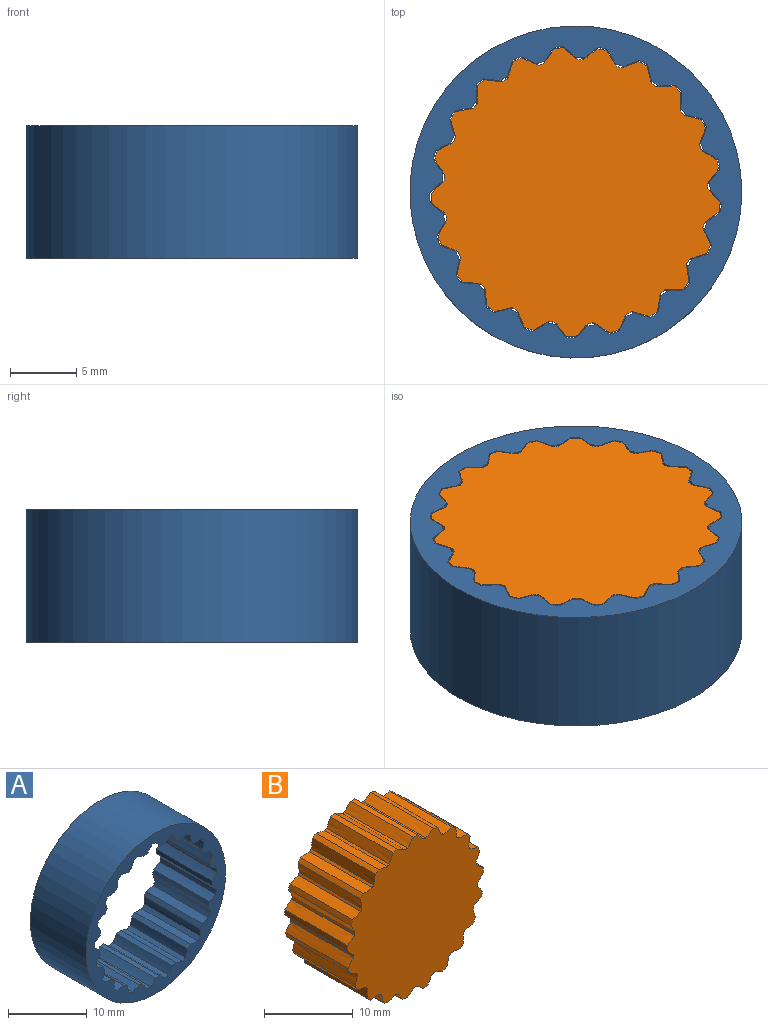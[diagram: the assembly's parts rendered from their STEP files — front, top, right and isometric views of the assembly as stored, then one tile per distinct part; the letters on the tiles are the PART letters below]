
ASSEMBLY  parts=2 mates=1
PART A: 87 faces, bbox 25x10x25 mm
  f0: cylinder r=10.11mm len=10mm, axis (0,1,0), area 6.9mm2, adj f20,f21,f38,f84
  f1: cylinder r=10.11mm len=10mm, axis (0,1,0), area 6.9mm2, adj f20,f21,f81,f86
  f2: cylinder r=10.11mm len=10mm, axis (0,1,0), area 6.9mm2, adj f20,f21,f78,f83
  f3: cylinder r=10.11mm len=10mm, axis (0,1,0), area 6.9mm2, adj f20,f21,f75,f80
  f4: cylinder r=10.11mm len=10mm, axis (0,1,0), area 6.9mm2, adj f20,f21,f72,f77
  f5: cylinder r=10.11mm len=10mm, axis (0,1,0), area 6.9mm2, adj f20,f21,f69,f74
  f6: cylinder r=10.11mm len=10mm, axis (0,1,0), area 6.9mm2, adj f20,f21,f66,f71
  f7: cylinder r=10.11mm len=10mm, axis (0,1,0), area 6.9mm2, adj f20,f21,f63,f68
  f8: cylinder r=10.11mm len=10mm, axis (0,1,0), area 6.9mm2, adj f20,f21,f60,f65
  f9: cylinder r=10.11mm len=10mm, axis (0,1,0), area 6.9mm2, adj f20,f21,f57,f62
  f10: cylinder r=10.11mm len=10mm, axis (0,1,0), area 6.9mm2, adj f20,f21,f54,f59
  f11: cylinder r=10.11mm len=10mm, axis (0,1,0), area 6.9mm2, adj f20,f21,f51,f56
  f12: cylinder r=10.11mm len=10mm, axis (0,1,0), area 6.9mm2, adj f20,f21,f48,f53
  f13: cylinder r=10.11mm len=10mm, axis (0,1,0), area 6.9mm2, adj f20,f21,f45,f50
  f14: cylinder r=10.11mm len=10mm, axis (0,1,0), area 6.9mm2, adj f20,f21,f42,f47
  f15: cylinder r=10.11mm len=10mm, axis (0,1,0), area 6.9mm2, adj f20,f21,f39,f44
  f16: cylinder r=10.11mm len=10mm, axis (0,1,0), area 6.9mm2, adj f20,f21,f35,f36
  f17: cylinder r=10.11mm len=10mm, axis (0,1,0), area 6.9mm2, adj f20,f21,f32,f33
  f18: cylinder r=10.11mm len=10mm, axis (0,1,0), area 6.9mm2, adj f20,f21,f26,f30
  f19: cylinder r=10.11mm len=10mm, axis (0,1,0), area 6.9mm2, adj f20,f21,f27,f41
  f20: plane 25x25mm, normal (0,-1,0), area 141.1mm2, adj f0,f1,f2,f3,f4,f5,f6,f7
  f21: plane 25x25mm, normal (0,1,0), area 141.1mm2, adj f0,f1,f2,f3,f4,f5,f6,f7
  f22: cylinder r=10.11mm len=10mm, axis (0,1,0), area 6.9mm2, adj f20,f21,f24,f29
  f23: cylinder r=12.5mm len=25mm, axis (0,1,0), area 785.4mm2, adj f20,f21
  f24: cylinder r=7.51mm len=10mm, axis (0,-1,0), area 12.7mm2, adj f20,f21,f22,f25
  f25: cylinder r=11mm len=10mm, axis (0,1,0), area 6.6mm2, adj f20,f21,f24,f26
  f26: cylinder r=7.51mm len=10mm, axis (0,1,0), area 12.7mm2, adj f18,f20,f21,f25
  f27: cylinder r=7.51mm len=10mm, axis (0,-1,0), area 12.7mm2, adj f19,f20,f21,f28
  f28: cylinder r=11mm len=10mm, axis (0,1,0), area 6.6mm2, adj f20,f21,f27,f29
  f29: cylinder r=7.51mm len=10mm, axis (0,1,0), area 12.7mm2, adj f20,f21,f22,f28
  f30: cylinder r=7.51mm len=10mm, axis (0,-1,0), area 12.7mm2, adj f18,f20,f21,f31
  f31: cylinder r=11mm len=10mm, axis (0,1,0), area 6.6mm2, adj f20,f21,f30,f32
  f32: cylinder r=7.51mm len=10mm, axis (0,1,0), area 12.7mm2, adj f17,f20,f21,f31
  f33: cylinder r=7.51mm len=10mm, axis (0,-1,0), area 12.7mm2, adj f17,f20,f21,f34
  f34: cylinder r=11mm len=10mm, axis (0,1,0), area 6.6mm2, adj f20,f21,f33,f35
  f35: cylinder r=7.51mm len=10mm, axis (0,1,0), area 12.7mm2, adj f16,f20,f21,f34
  f36: cylinder r=7.51mm len=10mm, axis (0,-1,0), area 12.7mm2, adj f16,f20,f21,f37
  f37: cylinder r=11mm len=10mm, axis (0,1,0), area 6.6mm2, adj f20,f21,f36,f38
  f38: cylinder r=7.51mm len=10mm, axis (0,1,0), area 12.7mm2, adj f0,f20,f21,f37
  f39: cylinder r=7.51mm len=10mm, axis (0,-1,0), area 12.7mm2, adj f15,f20,f21,f40
  f40: cylinder r=11mm len=10mm, axis (0,1,0), area 6.6mm2, adj f20,f21,f39,f41
  f41: cylinder r=7.51mm len=10mm, axis (0,1,0), area 12.7mm2, adj f19,f20,f21,f40
  f42: cylinder r=7.51mm len=10mm, axis (0,-1,0), area 12.7mm2, adj f14,f20,f21,f43
  f43: cylinder r=11mm len=10mm, axis (0,1,0), area 6.6mm2, adj f20,f21,f42,f44
  f44: cylinder r=7.51mm len=10mm, axis (0,1,0), area 12.7mm2, adj f15,f20,f21,f43
  f45: cylinder r=7.51mm len=10mm, axis (0,-1,0), area 12.7mm2, adj f13,f20,f21,f46
  f46: cylinder r=11mm len=10mm, axis (0,1,0), area 6.6mm2, adj f20,f21,f45,f47
  f47: cylinder r=7.51mm len=10mm, axis (0,1,0), area 12.7mm2, adj f14,f20,f21,f46
  f48: cylinder r=7.51mm len=10mm, axis (0,-1,0), area 12.7mm2, adj f12,f20,f21,f49
  f49: cylinder r=11mm len=10mm, axis (0,1,0), area 6.6mm2, adj f20,f21,f48,f50
  f50: cylinder r=7.51mm len=10mm, axis (0,1,0), area 12.7mm2, adj f13,f20,f21,f49
  f51: cylinder r=7.51mm len=10mm, axis (0,-1,0), area 12.7mm2, adj f11,f20,f21,f52
  f52: cylinder r=11mm len=10mm, axis (0,1,0), area 6.6mm2, adj f20,f21,f51,f53
  f53: cylinder r=7.51mm len=10mm, axis (0,1,0), area 12.7mm2, adj f12,f20,f21,f52
  f54: cylinder r=7.51mm len=10mm, axis (0,-1,0), area 12.7mm2, adj f10,f20,f21,f55
  f55: cylinder r=11mm len=10mm, axis (0,1,0), area 6.6mm2, adj f20,f21,f54,f56
  f56: cylinder r=7.51mm len=10mm, axis (0,1,0), area 12.7mm2, adj f11,f20,f21,f55
  f57: cylinder r=7.51mm len=10mm, axis (0,-1,0), area 12.7mm2, adj f9,f20,f21,f58
  f58: cylinder r=11mm len=10mm, axis (0,1,0), area 6.6mm2, adj f20,f21,f57,f59
  f59: cylinder r=7.51mm len=10mm, axis (0,1,0), area 12.7mm2, adj f10,f20,f21,f58
  f60: cylinder r=7.51mm len=10mm, axis (0,-1,0), area 12.7mm2, adj f8,f20,f21,f61
  f61: cylinder r=11mm len=10mm, axis (0,1,0), area 6.6mm2, adj f20,f21,f60,f62
  f62: cylinder r=7.51mm len=10mm, axis (0,1,0), area 12.7mm2, adj f9,f20,f21,f61
  f63: cylinder r=7.51mm len=10mm, axis (0,-1,0), area 12.7mm2, adj f7,f20,f21,f64
  f64: cylinder r=11mm len=10mm, axis (0,1,0), area 6.6mm2, adj f20,f21,f63,f65
  f65: cylinder r=7.51mm len=10mm, axis (0,1,0), area 12.7mm2, adj f8,f20,f21,f64
  f66: cylinder r=7.51mm len=10mm, axis (0,-1,0), area 12.7mm2, adj f6,f20,f21,f67
  f67: cylinder r=11mm len=10mm, axis (0,1,0), area 6.6mm2, adj f20,f21,f66,f68
  f68: cylinder r=7.51mm len=10mm, axis (0,1,0), area 12.7mm2, adj f7,f20,f21,f67
  f69: cylinder r=7.51mm len=10mm, axis (0,-1,0), area 12.7mm2, adj f5,f20,f21,f70
  f70: cylinder r=11mm len=10mm, axis (0,1,0), area 6.6mm2, adj f20,f21,f69,f71
  f71: cylinder r=7.51mm len=10mm, axis (0,1,0), area 12.7mm2, adj f6,f20,f21,f70
  f72: cylinder r=7.51mm len=10mm, axis (0,-1,0), area 12.7mm2, adj f4,f20,f21,f73
  f73: cylinder r=11mm len=10mm, axis (0,1,0), area 6.6mm2, adj f20,f21,f72,f74
  f74: cylinder r=7.51mm len=10mm, axis (0,1,0), area 12.7mm2, adj f5,f20,f21,f73
  f75: cylinder r=7.51mm len=10mm, axis (0,-1,0), area 12.7mm2, adj f3,f20,f21,f76
  f76: cylinder r=11mm len=10mm, axis (0,1,0), area 6.6mm2, adj f20,f21,f75,f77
  f77: cylinder r=7.51mm len=10mm, axis (0,1,0), area 12.7mm2, adj f4,f20,f21,f76
  f78: cylinder r=7.51mm len=10mm, axis (0,-1,0), area 12.7mm2, adj f2,f20,f21,f79
  f79: cylinder r=11mm len=10mm, axis (0,1,0), area 6.6mm2, adj f20,f21,f78,f80
  f80: cylinder r=7.51mm len=10mm, axis (0,1,0), area 12.7mm2, adj f3,f20,f21,f79
  f81: cylinder r=7.51mm len=10mm, axis (0,-1,0), area 12.7mm2, adj f1,f20,f21,f82
  f82: cylinder r=11mm len=10mm, axis (0,1,0), area 6.6mm2, adj f20,f21,f81,f83
  f83: cylinder r=7.51mm len=10mm, axis (0,1,0), area 12.7mm2, adj f2,f20,f21,f82
  f84: cylinder r=7.51mm len=10mm, axis (0,-1,0), area 12.7mm2, adj f0,f20,f21,f85
  f85: cylinder r=11mm len=10mm, axis (0,1,0), area 6.6mm2, adj f20,f21,f84,f86
  f86: cylinder r=7.51mm len=10mm, axis (0,1,0), area 12.7mm2, adj f1,f20,f21,f85
PART B: 86 faces, bbox 21.8x10x21.7 mm
  f0: cylinder r=9.95mm len=10mm, axis (0,1,0), area 3.6mm2, adj f21,f22,f25,f83
  f1: cylinder r=9.95mm len=10mm, axis (0,1,0), area 3.6mm2, adj f21,f22,f80,f85
  f2: cylinder r=9.95mm len=10mm, axis (0,1,0), area 3.6mm2, adj f21,f22,f77,f82
  f3: cylinder r=9.95mm len=10mm, axis (0,1,0), area 3.6mm2, adj f21,f22,f74,f79
  f4: cylinder r=9.95mm len=10mm, axis (0,1,0), area 3.6mm2, adj f21,f22,f71,f76
  f5: cylinder r=9.95mm len=10mm, axis (0,1,0), area 3.6mm2, adj f21,f22,f68,f73
  f6: cylinder r=9.95mm len=10mm, axis (0,1,0), area 3.6mm2, adj f21,f22,f65,f70
  f7: cylinder r=9.95mm len=10mm, axis (0,1,0), area 3.6mm2, adj f21,f22,f62,f67
  f8: cylinder r=9.95mm len=10mm, axis (0,1,0), area 3.6mm2, adj f21,f22,f59,f64
  f9: cylinder r=9.95mm len=10mm, axis (0,1,0), area 3.6mm2, adj f21,f22,f56,f61
  f10: cylinder r=9.95mm len=10mm, axis (0,1,0), area 3.6mm2, adj f21,f22,f53,f58
  f11: cylinder r=9.95mm len=10mm, axis (0,1,0), area 3.6mm2, adj f21,f22,f50,f55
  f12: cylinder r=9.95mm len=10mm, axis (0,1,0), area 3.6mm2, adj f21,f22,f47,f52
  f13: cylinder r=9.95mm len=10mm, axis (0,1,0), area 3.6mm2, adj f21,f22,f44,f49
  f14: cylinder r=9.95mm len=10mm, axis (0,1,0), area 3.6mm2, adj f21,f22,f41,f46
  f15: cylinder r=9.95mm len=10mm, axis (0,1,0), area 3.6mm2, adj f21,f22,f38,f43
  f16: cylinder r=9.95mm len=10mm, axis (0,1,0), area 3.6mm2, adj f21,f22,f35,f40
  f17: cylinder r=9.95mm len=10mm, axis (0,1,0), area 3.6mm2, adj f21,f22,f32,f37
  f18: cylinder r=9.95mm len=10mm, axis (0,1,0), area 3.6mm2, adj f21,f22,f29,f34
  f19: cylinder r=9.95mm len=10mm, axis (0,1,0), area 3.6mm2, adj f21,f22,f26,f31
  f20: cylinder r=9.95mm len=10mm, axis (0,1,0), area 3.6mm2, adj f21,f22,f23,f28
  f21: plane 21.78x21.73mm, normal (0,-1,0), area 343.1mm2, adj f0,f1,f2,f3,f4,f5,f6,f7
  f22: plane 21.78x21.73mm, normal (0,1,0), area 343.1mm2, adj f0,f1,f2,f3,f4,f5,f6,f7
  f23: extruded ~10x1.37mm, area 14.1mm2, adj f20,f21,f22,f24
  f24: cylinder r=10.9mm len=10mm, axis (0,1,0), area 6.9mm2, adj f21,f22,f23,f25
  f25: extruded ~10x1.39mm, area 14.1mm2, adj f0,f21,f22,f24
  f26: extruded ~10x1.22mm, area 14.1mm2, adj f19,f21,f22,f27
  f27: cylinder r=10.9mm len=10mm, axis (0,1,0), area 6.9mm2, adj f21,f22,f26,f28
  f28: extruded ~10x1.27mm, area 14.1mm2, adj f20,f21,f22,f27
  f29: extruded ~10x1.03mm, area 14.1mm2, adj f18,f21,f22,f30
  f30: cylinder r=10.9mm len=10mm, axis (0,1,0), area 6.9mm2, adj f21,f22,f29,f31
  f31: extruded ~10x1.03mm, area 14.1mm2, adj f19,f21,f22,f30
  f32: extruded ~10x1.27mm, area 14.1mm2, adj f17,f21,f22,f33
  f33: cylinder r=10.9mm len=10mm, axis (0,1,0), area 6.9mm2, adj f21,f22,f32,f34
  f34: extruded ~10x1.22mm, area 14.1mm2, adj f18,f21,f22,f33
  f35: extruded ~10x1.39mm, area 14.1mm2, adj f16,f21,f22,f36
  f36: cylinder r=10.9mm len=10mm, axis (0,1,0), area 6.9mm2, adj f21,f22,f35,f37
  f37: extruded ~10x1.37mm, area 14.1mm2, adj f17,f21,f22,f36
  f38: extruded ~10x1.39mm, area 14.1mm2, adj f15,f21,f22,f39
  f39: cylinder r=10.9mm len=10mm, axis (0,1,0), area 6.9mm2, adj f21,f22,f38,f40
  f40: extruded ~10x1.4mm, area 14.1mm2, adj f16,f21,f22,f39
  f41: extruded ~10x1.27mm, area 14.1mm2, adj f14,f21,f22,f42
  f42: cylinder r=10.9mm len=10mm, axis (0,1,0), area 6.9mm2, adj f21,f22,f41,f43
  f43: extruded ~10x1.31mm, area 14.1mm2, adj f15,f21,f22,f42
  f44: extruded ~10x1.03mm, area 14.1mm2, adj f13,f21,f22,f45
  f45: cylinder r=10.9mm len=10mm, axis (0,1,0), area 6.9mm2, adj f21,f22,f44,f46
  f46: extruded ~10x1.1mm, area 14.1mm2, adj f14,f21,f22,f45
  f47: extruded ~10x1.22mm, area 14.1mm2, adj f12,f21,f22,f48
  f48: cylinder r=10.9mm len=10mm, axis (0,1,0), area 6.9mm2, adj f21,f22,f47,f49
  f49: extruded ~10x1.17mm, area 14.1mm2, adj f13,f21,f22,f48
  f50: extruded ~10x1.37mm, area 14.1mm2, adj f11,f21,f22,f51
  f51: cylinder r=10.9mm len=10mm, axis (0,1,0), area 6.9mm2, adj f21,f22,f50,f52
  f52: extruded ~10x1.35mm, area 14.1mm2, adj f12,f21,f22,f51
  f53: extruded ~10x1.4mm, area 14.1mm2, adj f10,f21,f22,f54
  f54: cylinder r=10.9mm len=10mm, axis (0,1,0), area 6.9mm2, adj f21,f22,f53,f55
  f55: extruded ~10x1.41mm, area 14.1mm2, adj f11,f21,f22,f54
  f56: extruded ~10x1.31mm, area 14.1mm2, adj f9,f21,f22,f57
  f57: cylinder r=10.9mm len=10mm, axis (0,1,0), area 6.9mm2, adj f21,f22,f56,f58
  f58: extruded ~10x1.34mm, area 14.1mm2, adj f10,f21,f22,f57
  f59: extruded ~10x1.1mm, area 14.1mm2, adj f8,f21,f22,f60
  f60: cylinder r=10.9mm len=10mm, axis (0,1,0), area 6.9mm2, adj f21,f22,f59,f61
  f61: extruded ~10x1.16mm, area 14.1mm2, adj f9,f21,f22,f60
  f62: extruded ~10x1.16mm, area 14.1mm2, adj f7,f21,f22,f63
  f63: cylinder r=10.9mm len=10mm, axis (0,1,0), area 6.9mm2, adj f21,f22,f62,f64
  f64: extruded ~10x1.1mm, area 14.1mm2, adj f8,f21,f22,f63
  f65: extruded ~10x1.35mm, area 14.1mm2, adj f6,f21,f22,f66
  f66: cylinder r=10.9mm len=10mm, axis (0,1,0), area 6.9mm2, adj f21,f22,f65,f67
  f67: extruded ~10x1.31mm, area 14.1mm2, adj f7,f21,f22,f66
  f68: extruded ~10x1.41mm, area 14.1mm2, adj f5,f21,f22,f69
  f69: cylinder r=10.9mm len=10mm, axis (0,1,0), area 6.9mm2, adj f21,f22,f68,f70
  f70: extruded ~10x1.4mm, area 14.1mm2, adj f6,f21,f22,f69
  f71: extruded ~10x1.35mm, area 14.1mm2, adj f4,f21,f22,f72
  f72: cylinder r=10.9mm len=10mm, axis (0,1,0), area 6.9mm2, adj f21,f22,f71,f73
  f73: extruded ~10x1.37mm, area 14.1mm2, adj f5,f21,f22,f72
  f74: extruded ~10x1.16mm, area 14.1mm2, adj f3,f21,f22,f75
  f75: cylinder r=10.9mm len=10mm, axis (0,1,0), area 6.9mm2, adj f21,f22,f74,f76
  f76: extruded ~10x1.22mm, area 14.1mm2, adj f4,f21,f22,f75
  f77: extruded ~10x1.1mm, area 14.1mm2, adj f2,f21,f22,f78
  f78: cylinder r=10.9mm len=10mm, axis (0,1,0), area 6.9mm2, adj f21,f22,f77,f79
  f79: extruded ~10x1.04mm, area 14.1mm2, adj f3,f21,f22,f78
  f80: extruded ~10x1.31mm, area 14.1mm2, adj f1,f21,f22,f81
  f81: cylinder r=10.9mm len=10mm, axis (0,1,0), area 6.9mm2, adj f21,f22,f80,f82
  f82: extruded ~10x1.27mm, area 14.1mm2, adj f2,f21,f22,f81
  f83: extruded ~10x1.4mm, area 14.1mm2, adj f0,f21,f22,f84
  f84: cylinder r=10.9mm len=10mm, axis (0,1,0), area 6.9mm2, adj f21,f22,f83,f85
  f85: extruded ~10x1.39mm, area 14.1mm2, adj f1,f21,f22,f84
PLACE A rot(axis=(1,0,0),90deg) t=(-0.4,0.24,0.5)mm fixed
PLACE B rot(axis=(0.98,0.13,0.13),91deg) t=(-0.4,0.24,0.5)mm
MATE cylindrical B.f0 <-> A.f0  axis (0,0,1) through (-0.4,0.24,0.5)mm
